# Revit family: Franke_Cup_warmer_A-Series-A600_A800_A1000(EU,CH,GB)
name_source: partatom
category: Specialty Equipment
revit_build: Autodesk Revit 2015 (Build: 20140606_1530(x64)
units: mm (PartAtom-declared; Revit-internal decimal feet)

## types (2) — shared parameters
Assembly Code = key module  Cup warmer
Capacity = up to 120 cups
Cycle = 50 Hz
Cycle Alternative = 60 Hz
Depth (mm) = 453 mm  [stored 1.48622 ft]
Description = A-Series key module  Cup warmer
Energy loss acc. to DIN 18873 = -
Height (mm) = 585 mm  [stored 1.91929 ft]
Keynote = key module  Cup warmer
Manufacturer = Franke
Max Overcurrent Protection = -
Model = 410894 - Cup warmer A-Series - A600, A800, A1000
Number of Nutral Conductors = 1
Number of Poles = 1
Number of Protective Conductors = 1
URL = https://www.franke.com
Volts max. = 240 V
Volts min. = 220 V
Watts max. = 130 W
Watts min. = 110 W
Weight = 20 kg
Width (mm) = 270 mm  [stored 0.885827 ft]
zero-valued in all types: Cost

## per-type parameters (varying)
| type | Frontcover |
| Cup warmer A-Series-A600,A800,A1000(220-240V/black line/EU,CH,GB) | Franke Black |
| Cup warmer A-Series-A600,A800,A1000(220-240V/anthracite/EU,CH,GB) | Franke Anthracite |

note: [stored X ft] marks values corroborated as IEEE doubles in the binary element streams (Revit-internal decimal feet)
